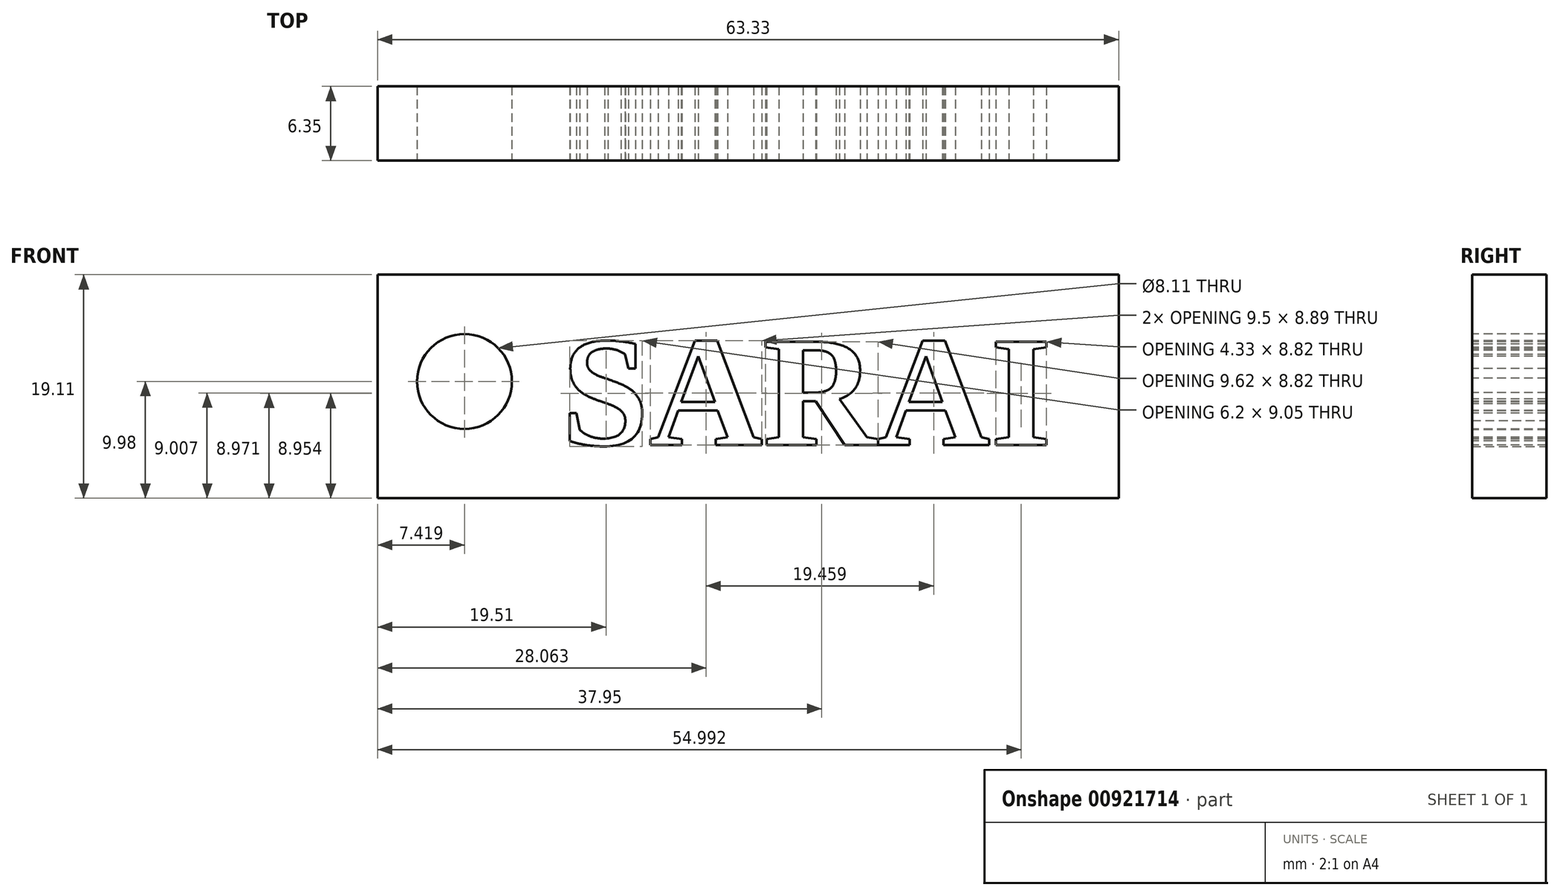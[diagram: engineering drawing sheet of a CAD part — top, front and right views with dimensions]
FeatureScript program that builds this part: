
annotation { "Feature Type Name" : "Feature", "Feature Type Description" : "" }
export const myFeature = defineFeature(function(context is Context, id is Id, definition is map)
    precondition{}
    {
        {
            var Q0;
            Q0=qCreatedBy(makeId("Front.planeOp"),FACE);
            var sketch = newSketch(context, id + "F0", { "sketchPlane" : qUnion([Q0])});
            skLineSegment(sketch, "E0.bottom", {"start": v(-29.8, 9.13) * mm, "end": v(33.52, 9.13) * mm});
            skLineSegment(sketch, "E0.top", {"start": v(-29.8, -9.98) * mm, "end": v(33.52, -9.98) * mm});
            skLineSegment(sketch, "E0.left", {"start": v(-29.8, 9.13) * mm, "end": v(-29.8, -9.98) * mm});
            skLineSegment(sketch, "E0.right", {"start": v(33.52, 9.13) * mm, "end": v(33.52, -9.98) * mm});
            skSolve(sketch);
        }
        {
            var Q0;
            Q0 = qSketchRegion(id + "F0", true);
            extrude(context, id + "F1", {"entities" : qUnion([Q0]), "depth" : 6.35 * mm, "offsetDistance" : 25.4 * mm});
        }
        {
            var Q0;
            Q0=makeQuery(id+"F1.opExtrude","CAP_FACE",FACE,{"disambiguationData":[OSD([sQuery(id+"F0.wireOp",EDGE,"E0.bottom"),sQuery(id+"F0.wireOp",EDGE,"E0.top"),sQuery(id+"F0.wireOp",EDGE,"E0.left"),sQuery(id+"F0.wireOp",EDGE,"E0.right")])],"isStart":false});
            var sketch = newSketch(context, id + "F2", { "sketchPlane" : qUnion([Q0])});
            skCircle(sketch, "E1", {"center": v(-22.4, 0) * mm, "radius": 4.05 * mm});
            skSolve(sketch);
        }
        {
            var Q0;
            Q0 = qSketchRegion(id + "F2", true);
            extrude(context, id + "F3", {"entities" : qUnion([Q0]), "operationType" : NewBodyOperationType.REMOVE, "oppositeDirection" : true, "depth" : 6.35 * mm, "offsetDistance" : 25.4 * mm});
        }
        {
            var Q0;
            Q0=makeQuery(id+"F1.opExtrude","CAP_FACE",FACE,{"disambiguationData":[OSD([sQuery(id+"F0.wireOp",EDGE,"E0.bottom"),sQuery(id+"F0.wireOp",EDGE,"E0.top"),sQuery(id+"F0.wireOp",EDGE,"E0.left"),sQuery(id+"F0.wireOp",EDGE,"E0.right")])],"isStart":false});
            var sketch = newSketch(context, id + "F4", { "sketchPlane" : qUnion([Q0])});
            skText(sketch, "E2", { "text": "SARAI", "fontName": "Tinos-Bold.ttf"});
            const initialGuessF4  = {"E2": [-0.01412, -0.00542, 1, 0, 0.0097]};
            skSetInitialGuess(sketch, initialGuessF4);
            skSolve(sketch);
        }
        {
            var Q0;
            Q0 = qSketchRegion(id + "F4", true);
            extrude(context, id + "F5", {"entities" : qUnion([Q0]), "operationType" : NewBodyOperationType.REMOVE, "oppositeDirection" : true, "depth" : 6.35 * mm, "offsetDistance" : 25.4 * mm});
        }
    });
